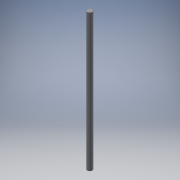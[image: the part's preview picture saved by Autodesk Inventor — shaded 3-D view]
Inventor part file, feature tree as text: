
AUTODESK INVENTOR PART (.ipt)
format: ipt  version: 2016 (Build 200138000, 138)  size: 105,984 bytes
history: native  units: in
note: dims shown in document units (in); Inventor stores cm internally (conversion verified against a paired STEP export)
features: direct_edit x1, chamfer x1, move_body x1
ambient origin geometry x8: Origin, YZ Plane, XZ Plane, XY Plane, X Axis, Y Axis, Z Axis, Center Point
bodies: Solid1 (feature_tree)
feature tree (3):
  direct_edit  "Direct Edit1"
  chamfer  "Chamfer1"  [1 undecoded]
  move_body  "Move1"
note: 1 required parameter value undecoded (feature->parameter linkage not recoverable at this tier; creation-order binding heuristic only, values carry confidence <= 0.55)
